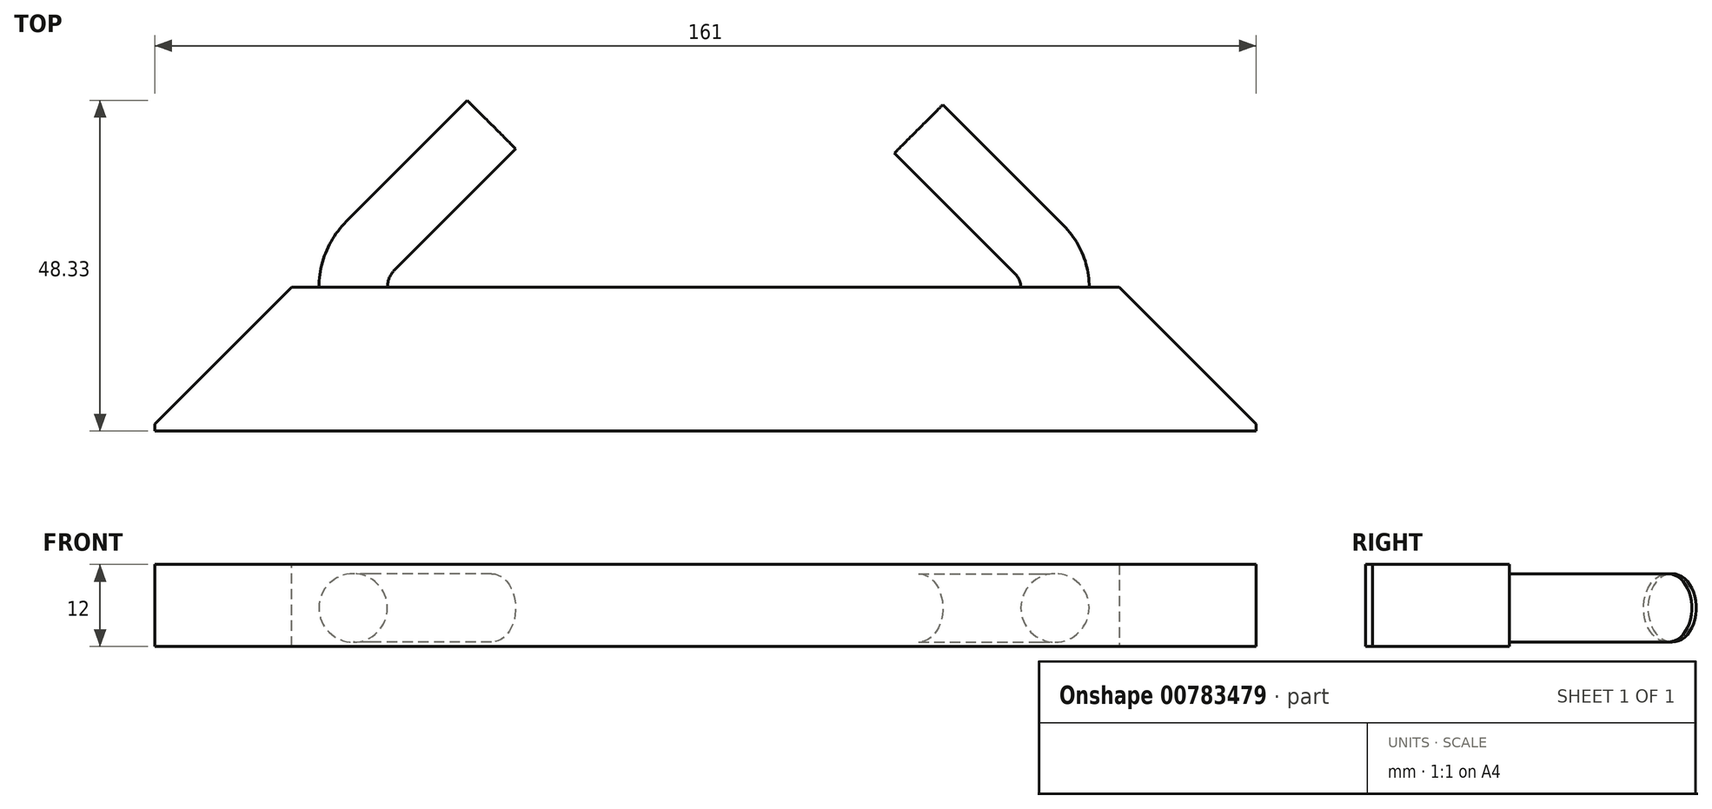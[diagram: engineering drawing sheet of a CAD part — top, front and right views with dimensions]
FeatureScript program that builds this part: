
annotation { "Feature Type Name" : "Feature", "Feature Type Description" : "" }
export const myFeature = defineFeature(function(context is Context, id is Id, definition is map)
    precondition{}
    {
        {
            var Q0;
            Q0=qCreatedBy(makeId("Top.planeOp"),FACE);
            var sketch = newSketch(context, id + "F0", { "sketchPlane" : qUnion([Q0])});
            skLineSegment(sketch, "E0.bottom", {"start": v(0, 0) * mm, "end": v(-161, 0) * mm});
            skLineSegment(sketch, "E0.top", {"start": v(0, -21) * mm, "end": v(-161, -21) * mm});
            skLineSegment(sketch, "E0.left", {"start": v(0, 0) * mm, "end": v(0, -21) * mm});
            skLineSegment(sketch, "E0.right", {"start": v(-161, 0) * mm, "end": v(-161, -21) * mm});
            skSolve(sketch);
        }
        {
            var Q0;
            Q0=makeQuery(id+"F0.imprint","IMPRINT",FACE,{"disambiguationData":[TD([[makeQuery(id+"F0.imprint","IMPRINT",EDGE,{"derivedFrom":sQuery(id+"F0.wireOp",EDGE,"E0.bottom")}),1.0]])]});
            extrude(context, id + "F1", {"entities" : qUnion([Q0]), "depth" : 12 * mm, "offsetDistance" : 25 * mm});
        }
        {
            var Q0;
            Q0=makeQuery(id+"F1.opExtrude","SWEPT_EDGE",EDGE,{"disambiguationData":[OSD([sQuery(id+"F0.wireOp",EDGE,"E0.bottom"),sQuery(id+"F0.wireOp",EDGE,"E0.right")])]});
            chamfer(context, id + "F2", {"entities" : qUnion([Q0]), "width" : 20 * mm});
        }
        {
            var Q0;
            Q0=makeQuery(id+"F1.opExtrude","SWEPT_EDGE",EDGE,{"disambiguationData":[OSD([sQuery(id+"F0.wireOp",EDGE,"E0.bottom"),sQuery(id+"F0.wireOp",EDGE,"E0.left")])]});
            chamfer(context, id + "F3", {"entities" : qUnion([Q0]), "width" : 20 * mm, "tangentPropagation" : true});
        }
        {
            var Q0;
            Q0=makeQuery(id+"F1.opExtrude","SWEPT_FACE",FACE,{"disambiguationData":[OSD([sQuery(id+"F0.wireOp",EDGE,"E0.bottom")])]});
            var sketch = newSketch(context, id + "F4", { "sketchPlane" : qUnion([Q0])});
            skCircle(sketch, "E1", {"center": v(132, 5.63) * mm, "radius": 5 * mm});
            skCircle(sketch, "E2", {"center": v(29.42, 5.63) * mm, "radius": 5 * mm});
            skSolve(sketch);
        }
        {
            var Q0;
            Q0=makeQuery(id+"F4.imprint","IMPRINT",FACE,{"disambiguationData":[TD([[makeQuery(id+"F4.imprint","IMPRINT",EDGE,{"derivedFrom":sQuery(id+"F4.wireOp",EDGE,"E1")}),-1.0]])]});
            var sketch = newSketch(context, id + "F5", { "sketchPlane" : qUnion([Q0])});
            skLineSegment(sketch, "E3", {"start": v(123.36, 11.86) * mm, "end": v(123.36, 0) * mm});
            skSolve(sketch);
        }
        {
            var Q0;
            Q0=makeQuery(id+"F5.imprint","IMPRINT",FACE,{"disambiguationData":[TD([[makeQuery(id+"F5.imprint","IMPRINT",EDGE,{"derivedFrom":makeQuery(id+"F4.imprint","IMPRINT",EDGE,{"derivedFrom":sQuery(id+"F4.wireOp",EDGE,"E1")})}),1.0]])]});
            var Q1;
            Q1=sQuery(id+"F5.wireOp",EDGE,"E3");
            revolve(context, id + "F6", {"operationType" : NewBodyOperationType.ADD, "surfaceOperationType" : NewSurfaceOperationType.NEW, "entities" : qUnion([Q0]), "axis" : qUnion([Q1]), "revolveType" : RevolveType.ONE_DIRECTION, "angle" : 45 * degree});
        }
        {
            var Q0;
            Q0=makeQuery(id+"F4.imprint","IMPRINT",FACE,{"disambiguationData":[TD([[makeQuery(id+"F4.imprint","IMPRINT",EDGE,{"derivedFrom":sQuery(id+"F4.wireOp",EDGE,"E1")}),-1.0]])]});
            var sketch = newSketch(context, id + "F7", { "sketchPlane" : qUnion([Q0])});
            skLineSegment(sketch, "E4", {"start": v(37.16, 11.74) * mm, "end": v(37.16, 0) * mm});
            skSolve(sketch);
        }
        {
            var Q0;
            Q0=makeQuery(id+"F4.imprint","IMPRINT",FACE,{"disambiguationData":[TD([[makeQuery(id+"F4.imprint","IMPRINT",EDGE,{"derivedFrom":sQuery(id+"F4.wireOp",EDGE,"E2")}),1.0]])]});
            var Q1;
            Q1=sQuery(id+"F7.wireOp",EDGE,"E4");
            revolve(context, id + "F8", {"operationType" : NewBodyOperationType.ADD, "surfaceOperationType" : NewSurfaceOperationType.NEW, "entities" : qUnion([Q0]), "axis" : qUnion([Q1]), "revolveType" : RevolveType.ONE_DIRECTION, "oppositeDirection" : true, "angle" : 45 * degree});
        }
        {
            var Q0;
            Q0=makeQuery(id+"F6.opRevolve","CAP_FACE",FACE,{"disambiguationData":[OSD([sQuery(id+"F4.wireOp",EDGE,"E1")])],"isStart":false});
            extrude(context, id + "F9", {"entities" : qUnion([Q0]), "operationType" : NewBodyOperationType.ADD, "depth" : 25 * mm, "offsetDistance" : 25 * mm});
        }
        {
            var Q0;
            Q0=makeQuery(id+"F8.opRevolve","CAP_FACE",FACE,{"disambiguationData":[OSD([sQuery(id+"F4.wireOp",EDGE,"E2")])],"isStart":false});
            extrude(context, id + "F10", {"entities" : qUnion([Q0]), "operationType" : NewBodyOperationType.ADD, "depth" : 25 * mm, "offsetDistance" : 25 * mm});
        }
    });
